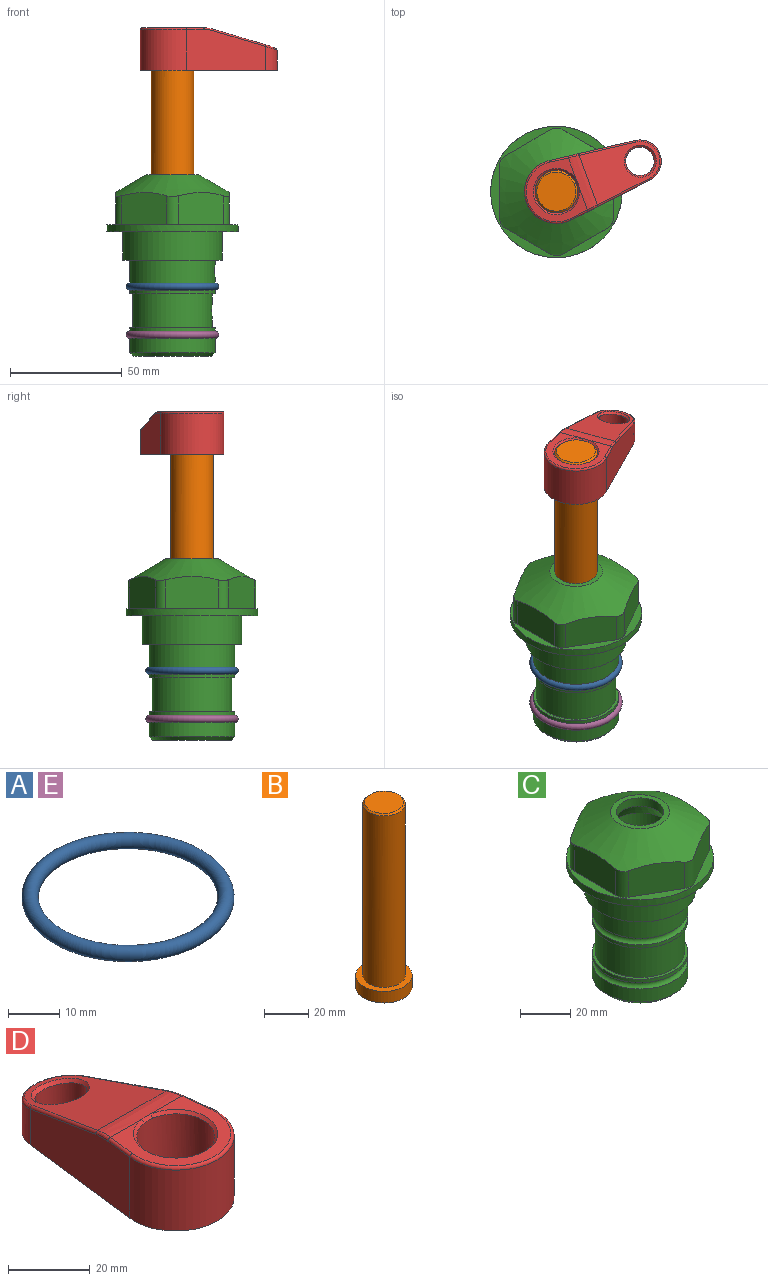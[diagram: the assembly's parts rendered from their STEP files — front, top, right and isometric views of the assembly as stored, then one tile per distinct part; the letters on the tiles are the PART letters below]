
ASSEMBLY  parts=5 mates=4
PART A: 1 faces, bbox 44.7x44.7x3.2 mm
  f0: torus R=19.05mm, axis (0,0,1), area 1193.9mm2
PART B: 6 faces, bbox 25.4x25.4x101.6 mm
  f0: plane 17.46x17.46mm, normal (0,0,1), area 239.5mm2, adj f5
  f1: plane 25.4x25.4mm, normal (0,0,-1), area 506.7mm2, adj f2
  f2: cylinder r=12.7mm len=25.4mm, axis (0,0,1), area 506.7mm2, adj f1,f3
  f3: plane 25.4x25.4mm, normal (0,0,1), area 221.7mm2, adj f2,f4
  f4: cylinder r=9.53mm len=94.46mm, axis (0,0,1), area 5653mm2, adj f3,f5
  f5: cone r=8.73mm half-angle=45deg, axis (0,0,-1), area 64.4mm2, adj f0,f4
PART C: 36 faces, bbox 58.7x58.7x81 mm
  f0: cylinder r=17.78mm len=35.56mm, axis (0,0,1), area 1670.8mm2, adj f23,f24,f31
  f1: cylinder r=19.05mm len=38.1mm, axis (0,0,1), area 1191.9mm2, adj f26,f27,f30
  f2: plane 58.66x58.66mm, normal (0,0,-1), area 1150.6mm2, adj f3,f28
  f3: cylinder r=29.33mm len=58.66mm, axis (0,0,-1), area 585.1mm2, adj f2,f4
  f4: plane 58.66x58.66mm, normal (0,0,1), area 475.9mm2, adj f3,f5,f6,f7,f8,f9,f10,f11
  f5: plane 20.32x14.34mm, normal (-0.5,0.87,0), area 324.4mm2, adj f4,f15,f16,f17
  f6: plane 20.32x14.34mm, normal (0.5,0.87,0), area 324.4mm2, adj f4,f14,f15,f17
  f7: plane 23.48x14.34mm, normal (1,0,0), area 324.4mm2, adj f4,f13,f14,f17
  f8: plane 20.32x14.34mm, normal (0.5,-0.87,0), area 324.4mm2, adj f4,f12,f13,f17
  f9: plane 20.32x14.34mm, normal (-0.5,-0.87,0), area 324.4mm2, adj f4,f11,f12,f17
  f10: plane 23.48x14.34mm, normal (-1,0,0), area 324.4mm2, adj f4,f11,f16,f17
  f11: cylinder r=5.08mm len=12.85mm, axis (0,0,-1), area 67.2mm2, adj f4,f9,f10,f17
  f12: cylinder r=5.08mm len=12.85mm, axis (0,0,-1), area 67.2mm2, adj f4,f8,f9,f17
  f13: cylinder r=5.08mm len=12.85mm, axis (0,0,-1), area 67.2mm2, adj f4,f7,f8,f17
  f14: cylinder r=5.08mm len=12.85mm, axis (0,0,-1), area 67.2mm2, adj f4,f6,f7,f17
  f15: cylinder r=5.08mm len=12.85mm, axis (0,0,-1), area 67.2mm2, adj f4,f5,f6,f17
  f16: cylinder r=5.08mm len=12.85mm, axis (0,0,-1), area 67.2mm2, adj f4,f5,f10,f17
  f17: cone r=11.73mm half-angle=60deg, axis (0,0,-1), area 2071.8mm2, adj f5,f6,f7,f8,f9,f10,f11,f12
  f18: plane 23.46x23.46mm, normal (0,0,1), area 147.4mm2, adj f17,f35
  f19: plane 34.93x34.93mm, normal (0,0,-1), area 958mm2, adj f29
  f20: cylinder r=19.05mm len=38.1mm, axis (0,0,1), area 760.1mm2, adj f21,f29
  f21: torus R=19.05mm, axis (0,0,1), area 565.3mm2, adj f20,f22
  f22: cylinder r=19.05mm len=38.1mm, axis (0,0,1), area 190mm2, adj f21,f23
  f23: plane 38.1x38.1mm, normal (0,0,1), area 146.9mm2, adj f0,f22
  f24: plane 38.1x38.1mm, normal (0,0,-1), area 146.9mm2, adj f0,f25
  f25: cylinder r=19.05mm len=38.1mm, axis (0,0,1), area 190mm2, adj f24,f26
  f26: torus R=19.05mm, axis (0,0,1), area 565.3mm2, adj f1,f25
  f27: plane 44.45x44.45mm, normal (0,0,-1), area 411.7mm2, adj f1,f28
  f28: cylinder r=22.23mm len=44.45mm, axis (0,0,1), area 1773.5mm2, adj f2,f27
  f29: cone r=19.05mm half-angle=45deg, axis (0,0,1), area 257.5mm2, adj f19,f20
  f30: cylinder r=3.17mm len=6.75mm, axis (-1,0,0), area 128mm2, adj f1,f33
  f31: cylinder r=3.17mm len=6.35mm, axis (-1,0,0), area 102.5mm2, adj f0,f33
  f32: plane 25.4x25.4mm, normal (0,0,1), area 506.7mm2, adj f33
  f33: cylinder r=12.7mm len=66.42mm, axis (0,0,-1), area 5236.2mm2, adj f30,f31,f32,f34
  f34: cone r=9.53mm half-angle=30deg, axis (0,0,-1), area 443.4mm2, adj f33,f35
  f35: cylinder r=9.53mm len=19.05mm, axis (0,0,-1), area 240.9mm2, adj f18,f34
PART D: 31 faces, bbox 31.7x65.5x19.8 mm
  f0: plane 39.12x18.26mm, normal (0.99,0.12,0), area 612.2mm2, adj f1,f4,f7,f11,f13,f15
  f1: cylinder r=9.53mm len=18.91mm, axis (0,0,-1), area 296.1mm2, adj f0,f2,f7,f17
  f2: plane 39.12x18.26mm, normal (-0.99,0.12,0), area 612.2mm2, adj f1,f4,f7,f12,f14,f16
  f3: cylinder r=6.35mm len=12.7mm, axis (0,0,-1), area 362.4mm2, adj f7,f18
  f4: cylinder r=14.29mm len=28.58mm, axis (0,0,-1), area 882.2mm2, adj f0,f2,f7,f10
  f5: cylinder r=9.53mm len=19.05mm, axis (0,0,-1), area 1092.6mm2, adj f7,f19,f20
  f6: plane 26.99x23.69mm, normal (0,0,1), area 216.2mm2, adj f9,f10,f11,f12,f19
  f7: plane 63.5x28.58mm, normal (0,0,-1), area 661.8mm2, adj f0,f1,f2,f3,f4,f5,f22,f23
  f8: plane 33.52x23.6mm, normal (0,0.26,0.97), area 486mm2, adj f9,f15,f16,f17,f18
  f9: cylinder r=19.05mm len=24.72mm, axis (1,0,0), area 120.4mm2, adj f6,f8,f13,f14,f20
  f10: torus R=13.49mm, axis (0,0,1), area 59mm2, adj f4,f6,f11,f12
  f11: cylinder r=0.79mm len=8.67mm, axis (0.12,-0.99,0), area 10.8mm2, adj f0,f6,f10,f13
  f12: cylinder r=0.79mm len=8.67mm, axis (0.12,0.99,0), area 10.8mm2, adj f2,f6,f10,f14
  f13: bspline ~4.95x1.42mm, area 6.1mm2, adj f0,f9,f11,f15
  f14: bspline ~4.95x1.42mm, area 6.1mm2, adj f2,f9,f12,f16
  f15: cylinder r=0.79mm len=25.95mm, axis (0.12,-0.96,0.26), area 32.9mm2, adj f0,f8,f13,f17
  f16: cylinder r=0.79mm len=25.95mm, axis (0.12,0.96,-0.26), area 32.9mm2, adj f2,f8,f14,f17
  f17: bspline ~18.91x8.38mm, area 30mm2, adj f1,f8,f15,f16
  f18: bspline ~14.29x14.29mm, area 48.3mm2, adj f3,f8
  f19: cone r=9.53mm half-angle=45deg, axis (0,0,1), area 66.5mm2, adj f5,f6,f20
  f20: bspline ~3.22x0.96mm, area 3.5mm2, adj f5,f9,f19
  f21: plane 2.75x2.72mm, normal (0,0,-1), area 2.9mm2, adj f23,f25,f28
  f22: plane 23.05x15.88mm, normal (-0.99,-0.12,0), area 323.6mm2, adj f7,f25,f26,f27,f28,f29
  f23: plane 23.05x15.88mm, normal (0.99,-0.12,0), area 323.6mm2, adj f7,f21,f25,f27,f28,f30
  f24: cylinder r=9.53mm len=10.69mm, axis (0,0,-1), area 114.7mm2, adj f7,f27,f29,f30
  f25: cylinder r=12.7mm len=20.59mm, axis (0,0,-1), area 381.1mm2, adj f7,f21,f22,f23,f26,f28
  f26: plane 2.75x2.72mm, normal (0,0,-1), area 2.9mm2, adj f22,f25,f28
  f27: plane 19.72x18.37mm, normal (0,-0.26,-0.97), area 291.8mm2, adj f22,f23,f24,f28,f29,f30
  f28: cylinder r=15.88mm len=19.92mm, axis (1,0,0), area 54.8mm2, adj f21,f22,f23,f25,f26,f27
  f29: cylinder r=1.59mm len=11mm, axis (0,0,-1), area 34.7mm2, adj f7,f22,f24,f27
  f30: cylinder r=1.59mm len=11mm, axis (0,0,-1), area 34.7mm2, adj f7,f23,f24,f27
PART E: same geometry as A
PLACE A at identity
PLACE B rot(axis=(0,0,-1),70deg) t=(0,0,27.55)mm
PLACE C at identity fixed
PLACE D rot(axis=(0,0,-1),70deg) t=(0,0,27.55)mm
PLACE E t=(0,0,-21.59)mm
MATE fastened E.f0 <-> C.f0  axis (0,0,1) through (0,0,-46.1)mm
MATE cylindrical B.f2 <-> C.f0  axis (0,0,-1) through (0,0,-10.55)mm
MATE fastened A.f0 <-> C.f0  axis (0,0,1) through (0,0,-24.51)mm
MATE fastened D.f4 <-> B.f2  axis (0,0,1) through (0,0,91.05)mm
